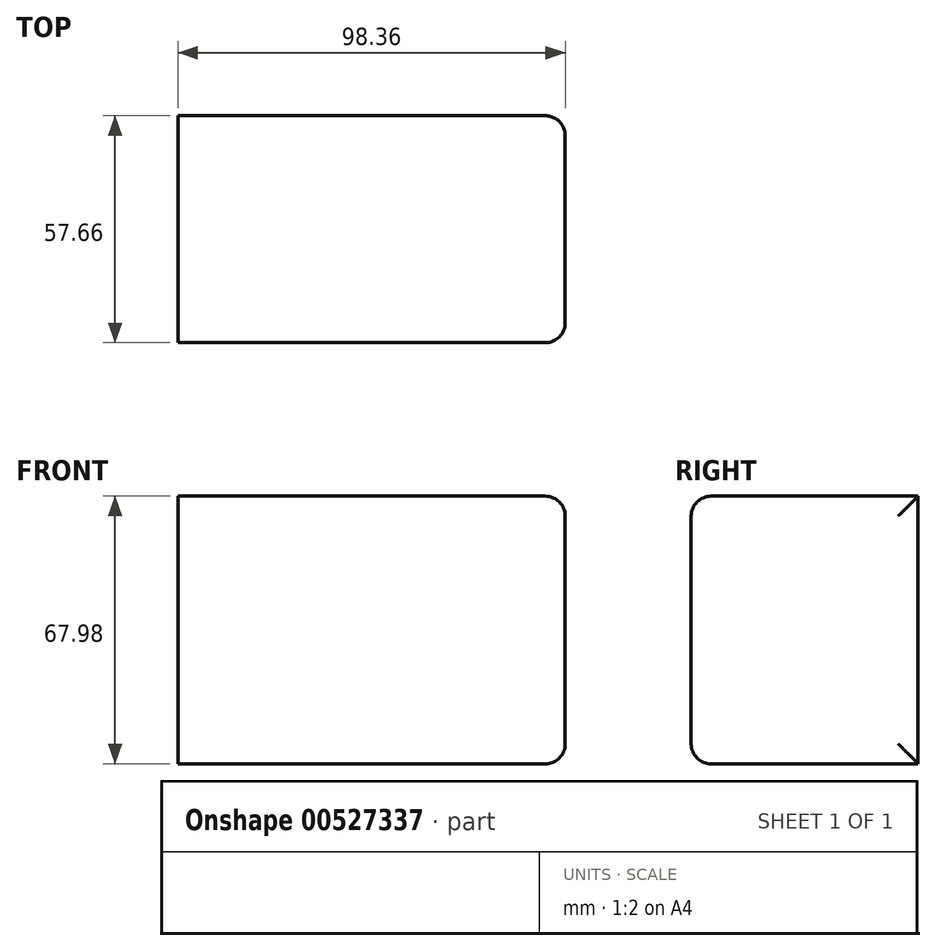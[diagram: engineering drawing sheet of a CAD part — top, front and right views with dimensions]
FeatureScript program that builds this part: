
annotation { "Feature Type Name" : "Feature", "Feature Type Description" : "" }
export const myFeature = defineFeature(function(context is Context, id is Id, definition is map)
    precondition{}
    {
        {
            var Q0;
            Q0=qCreatedBy(makeId("Front.planeOp"),FACE);
            var sketch = newSketch(context, id + "F0", { "sketchPlane" : qUnion([Q0])});
            skLineSegment(sketch, "E0.bottom", {"start": v(-46.62, 29.78) * mm, "end": v(51.74, 29.78) * mm});
            skLineSegment(sketch, "E0.top", {"start": v(-46.62, -38.2) * mm, "end": v(51.74, -38.2) * mm});
            skLineSegment(sketch, "E0.left", {"start": v(-46.62, 29.78) * mm, "end": v(-46.62, -38.2) * mm});
            skLineSegment(sketch, "E0.right", {"start": v(51.74, 29.78) * mm, "end": v(51.74, -38.2) * mm});
            skSolve(sketch);
        }
        {
            var Q0;
            Q0=makeQuery(id+"F0.imprint","IMPRINT",FACE,{"disambiguationData":[TD([[makeQuery(id+"F0.imprint","IMPRINT",EDGE,{"derivedFrom":sQuery(id+"F0.wireOp",EDGE,"E0.bottom")}),-1.0]])]});
            extrude(context, id + "F1", {"entities" : qUnion([Q0]), "depth" : 57.66 * mm, "offsetDistance" : 25.4 * mm});
        }
        {
            var Q0;
            Q0=makeQuery(id+"F1.opExtrude","CAP_EDGE",EDGE,{"disambiguationData":[OSD([sQuery(id+"F0.wireOp",EDGE,"E0.bottom")])],"isStart":false});
            var Q1;
            Q1=makeQuery(id+"F1.opExtrude","SWEPT_FACE",FACE,{"disambiguationData":[OSD([sQuery(id+"F0.wireOp",EDGE,"E0.right")])]});
            var Q2;
            Q2=makeQuery(id+"F1.opExtrude","CAP_EDGE",EDGE,{"disambiguationData":[OSD([sQuery(id+"F0.wireOp",EDGE,"E0.top")])],"isStart":false});
            fillet(context, id + "F2", {"entities" : qUnion([Q0, Q1, Q2]), "radius" : 5.08 * mm, "tangentPropagation" : true, "allowEdgeOverflow" : false});
        }
    });
